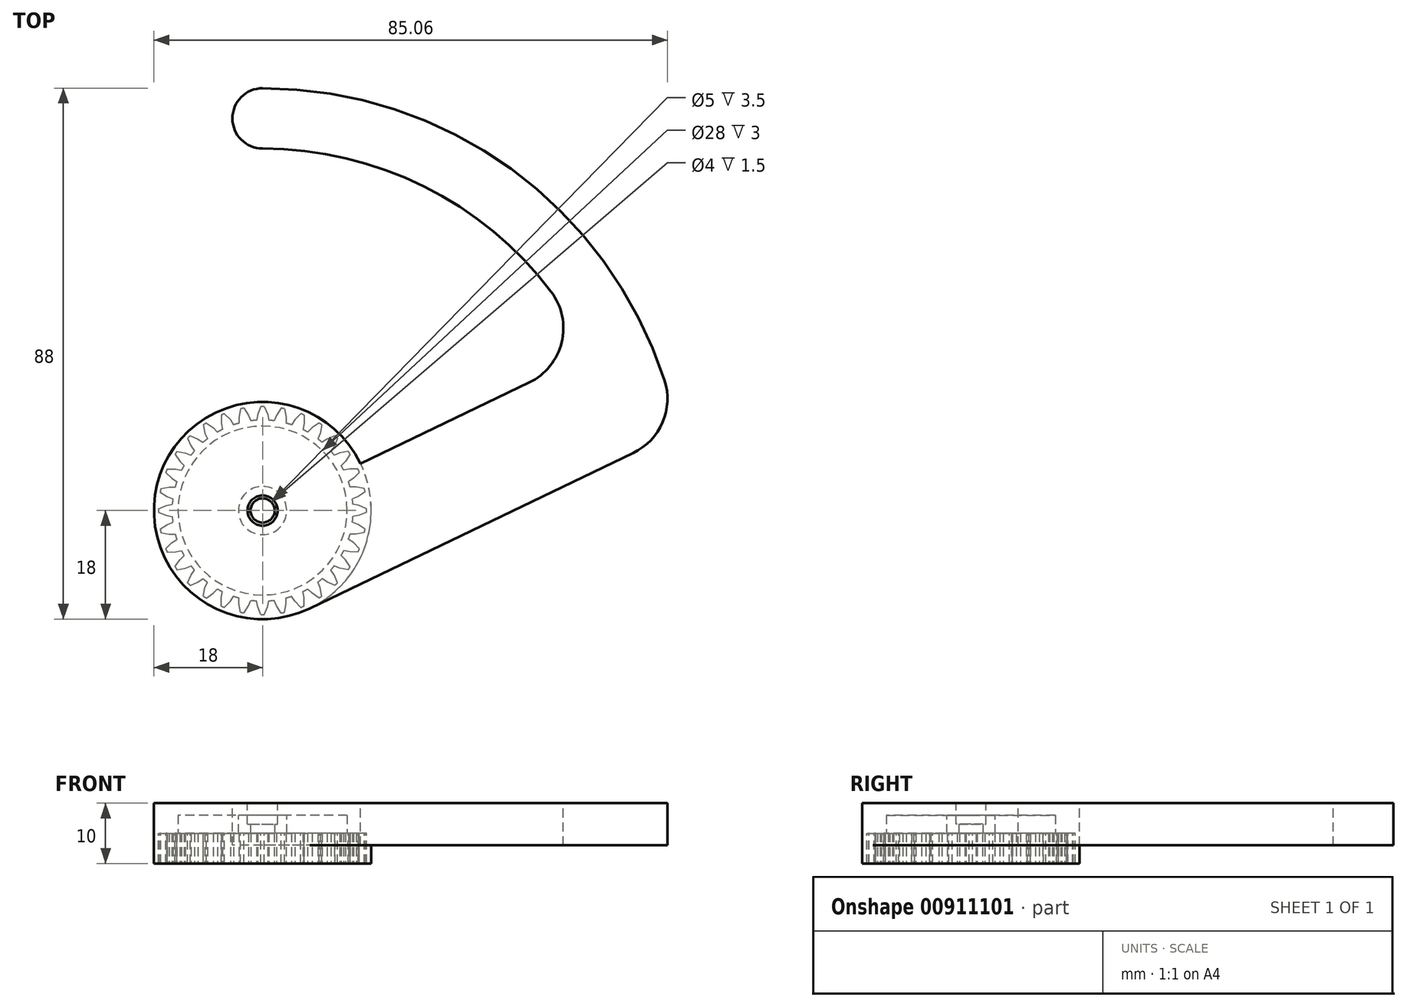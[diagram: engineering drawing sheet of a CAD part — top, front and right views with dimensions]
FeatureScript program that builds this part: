
annotation { "Feature Type Name" : "Feature", "Feature Type Description" : "" }
export const myFeature = defineFeature(function(context is Context, id is Id, definition is map)
    precondition{}
    {
        {
            var Q0;
            Q0=qCreatedBy(makeId("Top.planeOp"),FACE);
            var sketch = newSketch(context, id + "F0", { "sketchPlane" : qUnion([Q0])});
            skCircle(sketch, "E0", {"center": v(0, 0) * mm, "radius": 17.25 * mm});
            skCircle(sketch, "E1", {"center": v(0, 0) * mm, "radius": 15 * mm});
            skLineSegment(sketch, "E2", {"start": v(20.39, 0.01) * mm, "end": v(17.24, -0.58) * mm});
            skLineSegment(sketch, "E3", {"start": v(21.12, 1.29) * mm, "end": v(15.95, -0.82) * mm});
            skLineSegment(sketch, "E4", {"start": v(20.39, -0.02) * mm, "end": v(17.24, 0.58) * mm});
            skLineSegment(sketch, "E5", {"start": v(21.12, -1.29) * mm, "end": v(15.95, 0.82) * mm});
            skLineSegment(sketch, "E6", {"start": v(20, 4) * mm, "end": v(17.02, 2.8) * mm});
            skLineSegment(sketch, "E7", {"start": v(20.46, 5.38) * mm, "end": v(15.8, 2.3) * mm});
            skLineSegment(sketch, "E8", {"start": v(20, 3.96) * mm, "end": v(16.8, 3.93) * mm});
            skLineSegment(sketch, "E9", {"start": v(20.96, 2.85) * mm, "end": v(15.48, 3.92) * mm});
            skLineSegment(sketch, "E10", {"start": v(18.83, 7.81) * mm, "end": v(16.15, 6.06) * mm});
            skLineSegment(sketch, "E11", {"start": v(19.02, 9.27) * mm, "end": v(15.05, 5.34) * mm});
            skLineSegment(sketch, "E12", {"start": v(18.84, 7.79) * mm, "end": v(15.7, 7.13) * mm});
            skLineSegment(sketch, "E13", {"start": v(20, 6.89) * mm, "end": v(14.42, 6.86) * mm});
            skLineSegment(sketch, "E14", {"start": v(16.94, 11.34) * mm, "end": v(14.66, 9.1) * mm});
            skLineSegment(sketch, "E15", {"start": v(16.84, 12.8) * mm, "end": v(13.72, 8.18) * mm});
            skLineSegment(sketch, "E16", {"start": v(16.96, 11.31) * mm, "end": v(14.01, 10.06) * mm});
            skLineSegment(sketch, "E17", {"start": v(18.28, 10.66) * mm, "end": v(12.8, 9.54) * mm});
            skLineSegment(sketch, "E18", {"start": v(14.4, 14.43) * mm, "end": v(12.6, 11.78) * mm});
            skLineSegment(sketch, "E19", {"start": v(14.02, 15.84) * mm, "end": v(11.86, 10.7) * mm});
            skLineSegment(sketch, "E20", {"start": v(14.43, 14.4) * mm, "end": v(11.78, 12.6) * mm});
            skLineSegment(sketch, "E21", {"start": v(15.84, 14.02) * mm, "end": v(10.7, 11.86) * mm});
            skLineSegment(sketch, "E22", {"start": v(11.31, 16.96) * mm, "end": v(10.06, 14.01) * mm});
            skLineSegment(sketch, "E23", {"start": v(10.66, 18.28) * mm, "end": v(9.54, 12.8) * mm});
            skLineSegment(sketch, "E24", {"start": v(11.34, 16.94) * mm, "end": v(9.1, 14.66) * mm});
            skLineSegment(sketch, "E25", {"start": v(12.8, 16.84) * mm, "end": v(8.18, 13.72) * mm});
            skLineSegment(sketch, "E26", {"start": v(7.79, 18.84) * mm, "end": v(7.13, 15.7) * mm});
            skLineSegment(sketch, "E27", {"start": v(6.89, 20) * mm, "end": v(6.86, 14.42) * mm});
            skLineSegment(sketch, "E28", {"start": v(7.82, 18.83) * mm, "end": v(6.06, 16.15) * mm});
            skLineSegment(sketch, "E29", {"start": v(9.27, 19.02) * mm, "end": v(5.34, 15.05) * mm});
            skLineSegment(sketch, "E30", {"start": v(3.96, 20) * mm, "end": v(3.93, 16.8) * mm});
            skLineSegment(sketch, "E31", {"start": v(2.86, 20.96) * mm, "end": v(3.92, 15.48) * mm});
            skLineSegment(sketch, "E32", {"start": v(4, 20) * mm, "end": v(2.8, 17.02) * mm});
            skLineSegment(sketch, "E33", {"start": v(5.39, 20.46) * mm, "end": v(2.3, 15.8) * mm});
            skLineSegment(sketch, "E34", {"start": v(-0.01, 20.39) * mm, "end": v(0.58, 17.24) * mm});
            skLineSegment(sketch, "E35", {"start": v(-1.29, 21.12) * mm, "end": v(0.82, 15.95) * mm});
            skLineSegment(sketch, "E36", {"start": v(0.02, 20.39) * mm, "end": v(-0.58, 17.24) * mm});
            skLineSegment(sketch, "E37", {"start": v(1.3, 21.12) * mm, "end": v(-0.82, 15.95) * mm});
            skLineSegment(sketch, "E38", {"start": v(-4, 20) * mm, "end": v(-2.8, 17.02) * mm});
            skLineSegment(sketch, "E39", {"start": v(-5.38, 20.46) * mm, "end": v(-2.3, 15.8) * mm});
            skLineSegment(sketch, "E40", {"start": v(-3.96, 20) * mm, "end": v(-3.93, 16.8) * mm});
            skLineSegment(sketch, "E41", {"start": v(-2.85, 20.96) * mm, "end": v(-3.92, 15.48) * mm});
            skLineSegment(sketch, "E42", {"start": v(-7.82, 18.83) * mm, "end": v(-6.06, 16.15) * mm});
            skLineSegment(sketch, "E43", {"start": v(-9.27, 19.02) * mm, "end": v(-5.34, 15.05) * mm});
            skLineSegment(sketch, "E44", {"start": v(-7.79, 18.84) * mm, "end": v(-7.13, 15.7) * mm});
            skLineSegment(sketch, "E45", {"start": v(-6.89, 20) * mm, "end": v(-6.86, 14.42) * mm});
            skLineSegment(sketch, "E46", {"start": v(-11.34, 16.94) * mm, "end": v(-9.1, 14.66) * mm});
            skLineSegment(sketch, "E47", {"start": v(-12.8, 16.84) * mm, "end": v(-8.18, 13.72) * mm});
            skLineSegment(sketch, "E48", {"start": v(-11.31, 16.96) * mm, "end": v(-10.06, 14.01) * mm});
            skLineSegment(sketch, "E49", {"start": v(-10.66, 18.28) * mm, "end": v(-9.54, 12.8) * mm});
            skLineSegment(sketch, "E50", {"start": v(-14.43, 14.4) * mm, "end": v(-11.78, 12.6) * mm});
            skLineSegment(sketch, "E51", {"start": v(-15.84, 14.02) * mm, "end": v(-10.7, 11.86) * mm});
            skLineSegment(sketch, "E52", {"start": v(-14.4, 14.43) * mm, "end": v(-12.6, 11.78) * mm});
            skLineSegment(sketch, "E53", {"start": v(-14.02, 15.84) * mm, "end": v(-11.86, 10.7) * mm});
            skLineSegment(sketch, "E54", {"start": v(-16.96, 11.31) * mm, "end": v(-14.01, 10.06) * mm});
            skLineSegment(sketch, "E55", {"start": v(-18.27, 10.66) * mm, "end": v(-12.8, 9.54) * mm});
            skLineSegment(sketch, "E56", {"start": v(-16.94, 11.34) * mm, "end": v(-14.66, 9.1) * mm});
            skLineSegment(sketch, "E57", {"start": v(-16.84, 12.8) * mm, "end": v(-13.72, 8.18) * mm});
            skLineSegment(sketch, "E58", {"start": v(-18.84, 7.79) * mm, "end": v(-15.7, 7.13) * mm});
            skLineSegment(sketch, "E59", {"start": v(-20, 6.89) * mm, "end": v(-14.42, 6.86) * mm});
            skLineSegment(sketch, "E60", {"start": v(-18.83, 7.82) * mm, "end": v(-16.15, 6.06) * mm});
            skLineSegment(sketch, "E61", {"start": v(-19.02, 9.27) * mm, "end": v(-15.05, 5.34) * mm});
            skLineSegment(sketch, "E62", {"start": v(-20, 3.96) * mm, "end": v(-16.8, 3.93) * mm});
            skLineSegment(sketch, "E63", {"start": v(-20.96, 2.85) * mm, "end": v(-15.48, 3.92) * mm});
            skLineSegment(sketch, "E64", {"start": v(-20, 4) * mm, "end": v(-17.02, 2.8) * mm});
            skLineSegment(sketch, "E65", {"start": v(-20.46, 5.38) * mm, "end": v(-15.8, 2.3) * mm});
            skLineSegment(sketch, "E66", {"start": v(-20.39, -0.02) * mm, "end": v(-17.24, 0.58) * mm});
            skLineSegment(sketch, "E67", {"start": v(-21.12, -1.29) * mm, "end": v(-15.95, 0.82) * mm});
            skLineSegment(sketch, "E68", {"start": v(-20.39, 0.01) * mm, "end": v(-17.24, -0.58) * mm});
            skLineSegment(sketch, "E69", {"start": v(-21.12, 1.29) * mm, "end": v(-15.95, -0.82) * mm});
            skLineSegment(sketch, "E70", {"start": v(-20, -4) * mm, "end": v(-17.02, -2.8) * mm});
            skLineSegment(sketch, "E71", {"start": v(-20.46, -5.38) * mm, "end": v(-15.8, -2.3) * mm});
            skLineSegment(sketch, "E72", {"start": v(-20, -3.96) * mm, "end": v(-16.8, -3.93) * mm});
            skLineSegment(sketch, "E73", {"start": v(-20.96, -2.85) * mm, "end": v(-15.48, -3.92) * mm});
            skLineSegment(sketch, "E74", {"start": v(-18.83, -7.81) * mm, "end": v(-16.15, -6.06) * mm});
            skLineSegment(sketch, "E75", {"start": v(-19.02, -9.27) * mm, "end": v(-15.05, -5.34) * mm});
            skLineSegment(sketch, "E76", {"start": v(-18.84, -7.79) * mm, "end": v(-15.7, -7.13) * mm});
            skLineSegment(sketch, "E77", {"start": v(-20, -6.89) * mm, "end": v(-14.42, -6.86) * mm});
            skLineSegment(sketch, "E78", {"start": v(-16.94, -11.34) * mm, "end": v(-14.66, -9.1) * mm});
            skLineSegment(sketch, "E79", {"start": v(-16.84, -12.8) * mm, "end": v(-13.72, -8.18) * mm});
            skLineSegment(sketch, "E80", {"start": v(-16.96, -11.31) * mm, "end": v(-14.01, -10.06) * mm});
            skLineSegment(sketch, "E81", {"start": v(-18.27, -10.66) * mm, "end": v(-12.8, -9.54) * mm});
            skLineSegment(sketch, "E82", {"start": v(-14.4, -14.43) * mm, "end": v(-12.6, -11.78) * mm});
            skLineSegment(sketch, "E83", {"start": v(-14.02, -15.84) * mm, "end": v(-11.86, -10.7) * mm});
            skLineSegment(sketch, "E84", {"start": v(-14.43, -14.4) * mm, "end": v(-11.78, -12.6) * mm});
            skLineSegment(sketch, "E85", {"start": v(-15.84, -14.02) * mm, "end": v(-10.7, -11.86) * mm});
            skLineSegment(sketch, "E86", {"start": v(-11.31, -16.96) * mm, "end": v(-10.06, -14.01) * mm});
            skLineSegment(sketch, "E87", {"start": v(-10.66, -18.27) * mm, "end": v(-9.54, -12.8) * mm});
            skLineSegment(sketch, "E88", {"start": v(-11.34, -16.94) * mm, "end": v(-9.1, -14.66) * mm});
            skLineSegment(sketch, "E89", {"start": v(-12.8, -16.84) * mm, "end": v(-8.18, -13.72) * mm});
            skLineSegment(sketch, "E90", {"start": v(-7.79, -18.84) * mm, "end": v(-7.13, -15.7) * mm});
            skLineSegment(sketch, "E91", {"start": v(-6.89, -20) * mm, "end": v(-6.86, -14.42) * mm});
            skLineSegment(sketch, "E92", {"start": v(-7.81, -18.83) * mm, "end": v(-6.06, -16.15) * mm});
            skLineSegment(sketch, "E93", {"start": v(-9.27, -19.02) * mm, "end": v(-5.34, -15.05) * mm});
            skLineSegment(sketch, "E94", {"start": v(-3.96, -20) * mm, "end": v(-3.93, -16.8) * mm});
            skLineSegment(sketch, "E95", {"start": v(-2.86, -20.96) * mm, "end": v(-3.92, -15.48) * mm});
            skLineSegment(sketch, "E96", {"start": v(-4, -20) * mm, "end": v(-2.8, -17.02) * mm});
            skLineSegment(sketch, "E97", {"start": v(-5.38, -20.46) * mm, "end": v(-2.3, -15.8) * mm});
            skLineSegment(sketch, "E98", {"start": v(0.02, -20.39) * mm, "end": v(-0.58, -17.24) * mm});
            skLineSegment(sketch, "E99", {"start": v(1.29, -21.12) * mm, "end": v(-0.82, -15.95) * mm});
            skLineSegment(sketch, "E100", {"start": v(-0.01, -20.39) * mm, "end": v(0.58, -17.24) * mm});
            skLineSegment(sketch, "E101", {"start": v(-1.29, -21.12) * mm, "end": v(0.82, -15.95) * mm});
            skLineSegment(sketch, "E102", {"start": v(4, -20) * mm, "end": v(2.8, -17.02) * mm});
            skLineSegment(sketch, "E103", {"start": v(5.38, -20.46) * mm, "end": v(2.3, -15.8) * mm});
            skLineSegment(sketch, "E104", {"start": v(3.96, -20) * mm, "end": v(3.93, -16.8) * mm});
            skLineSegment(sketch, "E105", {"start": v(2.86, -20.96) * mm, "end": v(3.92, -15.48) * mm});
            skLineSegment(sketch, "E106", {"start": v(7.82, -18.83) * mm, "end": v(6.06, -16.15) * mm});
            skLineSegment(sketch, "E107", {"start": v(9.27, -19.02) * mm, "end": v(5.34, -15.05) * mm});
            skLineSegment(sketch, "E108", {"start": v(7.79, -18.84) * mm, "end": v(7.13, -15.7) * mm});
            skLineSegment(sketch, "E109", {"start": v(6.89, -20) * mm, "end": v(6.86, -14.42) * mm});
            skLineSegment(sketch, "E110", {"start": v(11.34, -16.94) * mm, "end": v(9.1, -14.66) * mm});
            skLineSegment(sketch, "E111", {"start": v(12.8, -16.84) * mm, "end": v(8.18, -13.72) * mm});
            skLineSegment(sketch, "E112", {"start": v(11.31, -16.96) * mm, "end": v(10.06, -14.01) * mm});
            skLineSegment(sketch, "E113", {"start": v(10.66, -18.28) * mm, "end": v(9.54, -12.8) * mm});
            skLineSegment(sketch, "E114", {"start": v(14.43, -14.4) * mm, "end": v(11.78, -12.6) * mm});
            skLineSegment(sketch, "E115", {"start": v(15.84, -14.02) * mm, "end": v(10.7, -11.86) * mm});
            skLineSegment(sketch, "E116", {"start": v(14.4, -14.43) * mm, "end": v(12.6, -11.78) * mm});
            skLineSegment(sketch, "E117", {"start": v(14.02, -15.84) * mm, "end": v(11.86, -10.7) * mm});
            skLineSegment(sketch, "E118", {"start": v(16.96, -11.31) * mm, "end": v(14.01, -10.06) * mm});
            skLineSegment(sketch, "E119", {"start": v(18.27, -10.66) * mm, "end": v(12.8, -9.54) * mm});
            skLineSegment(sketch, "E120", {"start": v(16.94, -11.34) * mm, "end": v(14.66, -9.1) * mm});
            skLineSegment(sketch, "E121", {"start": v(16.84, -12.8) * mm, "end": v(13.72, -8.18) * mm});
            skLineSegment(sketch, "E122", {"start": v(18.84, -7.79) * mm, "end": v(15.7, -7.13) * mm});
            skLineSegment(sketch, "E123", {"start": v(20, -6.89) * mm, "end": v(14.42, -6.86) * mm});
            skLineSegment(sketch, "E124", {"start": v(18.83, -7.81) * mm, "end": v(16.15, -6.06) * mm});
            skLineSegment(sketch, "E125", {"start": v(19.02, -9.27) * mm, "end": v(15.05, -5.34) * mm});
            skLineSegment(sketch, "E126", {"start": v(20, -3.96) * mm, "end": v(16.8, -3.93) * mm});
            skLineSegment(sketch, "E127", {"start": v(20.96, -2.86) * mm, "end": v(15.48, -3.92) * mm});
            skLineSegment(sketch, "E128", {"start": v(20, -4) * mm, "end": v(17.02, -2.8) * mm});
            skLineSegment(sketch, "E129", {"start": v(20.46, -5.38) * mm, "end": v(15.8, -2.3) * mm});
            skLineSegment(sketch, "E130.trimOffspring", {"start": v(-6.86, 14.42) * mm, "end": v(-5.74, 9.05) * mm});
            skLineSegment(sketch, "E131.trimOffspring", {"start": v(-6.86, 13.34) * mm, "end": v(-6.84, 10) * mm});
            skLineSegment(sketch, "E132.trimOffspring", {"start": v(-5.34, 15.05) * mm, "end": v(-2.34, 10.46) * mm});
            skLineSegment(sketch, "E133.trimOffspring", {"start": v(-4.58, 14.28) * mm, "end": v(-2.23, 11.91) * mm});
            skLineSegment(sketch, "E134.trimOffspring", {"start": v(-3.92, 15.48) * mm, "end": v(-3.87, 10) * mm});
            skLineSegment(sketch, "E135.trimOffspring", {"start": v(-4.12, 14.42) * mm, "end": v(-4.76, 11.15) * mm});
            skLineSegment(sketch, "E136.trimOffspring", {"start": v(-7.28, 13.11) * mm, "end": v(-4.52, 11.25) * mm});
            skLineSegment(sketch, "E137.trimOffspring", {"start": v(-8.18, 13.72) * mm, "end": v(-4.34, 9.8) * mm});
            skLineSegment(sketch, "E138.trimOffspring", {"start": v(-2.3, 15.8) * mm, "end": v(-0.25, 10.72) * mm});
            skLineSegment(sketch, "E139.trimOffspring", {"start": v(-1.7, 14.9) * mm, "end": v(0.13, 12.12) * mm});
            skLineSegment(sketch, "E140.trimOffspring", {"start": v(-0.82, 15.95) * mm, "end": v(-1.84, 10.56) * mm});
            skLineSegment(sketch, "E141.trimOffspring", {"start": v(-1.23, 14.95) * mm, "end": v(-2.5, 11.86) * mm});
            skLineSegment(sketch, "E142.trimOffspring", {"start": v(0.82, 15.95) * mm, "end": v(1.84, 10.56) * mm});
            skLineSegment(sketch, "E143.trimOffspring", {"start": v(1.23, 14.95) * mm, "end": v(2.5, 11.86) * mm});
            skLineSegment(sketch, "E144.trimOffspring", {"start": v(1.7, 14.9) * mm, "end": v(-0.13, 12.12) * mm});
            skLineSegment(sketch, "E145.trimOffspring", {"start": v(2.3, 15.8) * mm, "end": v(0.26, 10.72) * mm});
            skLineSegment(sketch, "E146.trimOffspring", {"start": v(3.92, 15.48) * mm, "end": v(3.87, 10) * mm});
            skLineSegment(sketch, "E147.trimOffspring", {"start": v(4.12, 14.42) * mm, "end": v(4.76, 11.15) * mm});
            skLineSegment(sketch, "E148.trimOffspring", {"start": v(4.58, 14.28) * mm, "end": v(2.23, 11.91) * mm});
            skLineSegment(sketch, "E149.trimOffspring", {"start": v(5.34, 15.05) * mm, "end": v(2.34, 10.46) * mm});
            skLineSegment(sketch, "E150.trimOffspring", {"start": v(6.86, 14.42) * mm, "end": v(5.74, 9.05) * mm});
            skLineSegment(sketch, "E151.trimOffspring", {"start": v(6.86, 13.34) * mm, "end": v(6.84, 10) * mm});
            skLineSegment(sketch, "E152.trimOffspring", {"start": v(7.28, 13.11) * mm, "end": v(4.52, 11.25) * mm});
            skLineSegment(sketch, "E153.trimOffspring", {"start": v(8.18, 13.72) * mm, "end": v(4.34, 9.8) * mm});
            skLineSegment(sketch, "E154.trimOffspring", {"start": v(9.54, 12.8) * mm, "end": v(7.4, 7.76) * mm});
            skLineSegment(sketch, "E155.trimOffspring", {"start": v(9.33, 11.75) * mm, "end": v(8.66, 8.48) * mm});
            skLineSegment(sketch, "E156.trimOffspring", {"start": v(9.7, 11.44) * mm, "end": v(6.62, 10.15) * mm});
            skLineSegment(sketch, "E157.trimOffspring", {"start": v(10.7, 11.86) * mm, "end": v(6.17, 8.77) * mm});
            skLineSegment(sketch, "E158.trimOffspring", {"start": v(11.86, 10.7) * mm, "end": v(8.77, 6.16) * mm});
            skLineSegment(sketch, "E159.trimOffspring", {"start": v(11.44, 9.7) * mm, "end": v(10.15, 6.62) * mm});
            skLineSegment(sketch, "E160.trimOffspring", {"start": v(11.75, 9.33) * mm, "end": v(8.48, 8.66) * mm});
            skLineSegment(sketch, "E161.trimOffspring", {"start": v(12.8, 9.54) * mm, "end": v(7.76, 7.4) * mm});
            skLineSegment(sketch, "E162.trimOffspring", {"start": v(-9.54, 12.8) * mm, "end": v(-7.4, 7.76) * mm});
            skLineSegment(sketch, "E163.trimOffspring", {"start": v(-9.33, 11.75) * mm, "end": v(-8.66, 8.48) * mm});
            skLineSegment(sketch, "E164.trimOffspring", {"start": v(-10.7, 11.86) * mm, "end": v(-6.16, 8.77) * mm});
            skLineSegment(sketch, "E165.trimOffspring", {"start": v(-9.7, 11.44) * mm, "end": v(-6.62, 10.15) * mm});
            skLineSegment(sketch, "E166.trimOffspring", {"start": v(-11.86, 10.7) * mm, "end": v(-8.77, 6.17) * mm});
            skLineSegment(sketch, "E167.trimOffspring", {"start": v(-11.44, 9.7) * mm, "end": v(-10.15, 6.62) * mm});
            skLineSegment(sketch, "E168.trimOffspring", {"start": v(-11.75, 9.33) * mm, "end": v(-8.48, 8.66) * mm});
            skLineSegment(sketch, "E169.trimOffspring", {"start": v(-12.8, 9.54) * mm, "end": v(-7.76, 7.4) * mm});
            skLineSegment(sketch, "E170.trimOffspring", {"start": v(-13.72, 8.18) * mm, "end": v(-9.8, 4.34) * mm});
            skLineSegment(sketch, "E171.trimOffspring", {"start": v(-13.11, 7.28) * mm, "end": v(-11.25, 4.52) * mm});
            skLineSegment(sketch, "E172.trimOffspring", {"start": v(-13.34, 6.86) * mm, "end": v(-10, 6.84) * mm});
            skLineSegment(sketch, "E173.trimOffspring", {"start": v(-14.42, 6.86) * mm, "end": v(-9.05, 5.74) * mm});
            skLineSegment(sketch, "E174.trimOffspring", {"start": v(-14.28, 4.58) * mm, "end": v(-11.91, 2.23) * mm});
            skLineSegment(sketch, "E175.trimOffspring", {"start": v(-15.05, 5.34) * mm, "end": v(-10.46, 2.34) * mm});
            skLineSegment(sketch, "E176.trimOffspring", {"start": v(-14.42, 4.12) * mm, "end": v(-11.15, 4.76) * mm});
            skLineSegment(sketch, "E177.trimOffspring", {"start": v(-15.48, 3.92) * mm, "end": v(-10, 3.87) * mm});
            skLineSegment(sketch, "E178.trimOffspring", {"start": v(-14.9, 1.7) * mm, "end": v(-12.12, -0.13) * mm});
            skLineSegment(sketch, "E179.trimOffspring", {"start": v(-15.8, 2.3) * mm, "end": v(-10.72, 0.25) * mm});
            skLineSegment(sketch, "E180.trimOffspring", {"start": v(-15.95, 0.82) * mm, "end": v(-10.56, 1.84) * mm});
            skLineSegment(sketch, "E181.trimOffspring", {"start": v(-14.95, 1.23) * mm, "end": v(-11.86, 2.5) * mm});
            skLineSegment(sketch, "E182.trimOffspring", {"start": v(13.72, 8.18) * mm, "end": v(9.8, 4.34) * mm});
            skLineSegment(sketch, "E183.trimOffspring", {"start": v(13.11, 7.28) * mm, "end": v(11.25, 4.52) * mm});
            skLineSegment(sketch, "E184.trimOffspring", {"start": v(13.34, 6.86) * mm, "end": v(10, 6.84) * mm});
            skLineSegment(sketch, "E185.trimOffspring", {"start": v(14.42, 6.86) * mm, "end": v(9.05, 5.74) * mm});
            skLineSegment(sketch, "E186.trimOffspring", {"start": v(15.05, 5.34) * mm, "end": v(10.46, 2.34) * mm});
            skLineSegment(sketch, "E187.trimOffspring", {"start": v(14.28, 4.58) * mm, "end": v(11.91, 2.23) * mm});
            skLineSegment(sketch, "E188.trimOffspring", {"start": v(14.42, 4.12) * mm, "end": v(11.15, 4.76) * mm});
            skLineSegment(sketch, "E189.trimOffspring", {"start": v(15.48, 3.92) * mm, "end": v(10, 3.87) * mm});
            skLineSegment(sketch, "E190.trimOffspring", {"start": v(15.8, 2.3) * mm, "end": v(10.72, 0.25) * mm});
            skLineSegment(sketch, "E191.trimOffspring", {"start": v(14.9, 1.7) * mm, "end": v(12.12, -0.13) * mm});
            skLineSegment(sketch, "E192.trimOffspring", {"start": v(14.95, 1.23) * mm, "end": v(11.86, 2.5) * mm});
            skLineSegment(sketch, "E193.trimOffspring", {"start": v(15.95, 0.82) * mm, "end": v(10.56, 1.84) * mm});
            skLineSegment(sketch, "E194.trimOffspring", {"start": v(15.95, -0.82) * mm, "end": v(10.56, -1.84) * mm});
            skLineSegment(sketch, "E195.trimOffspring", {"start": v(14.95, -1.23) * mm, "end": v(11.86, -2.5) * mm});
            skLineSegment(sketch, "E196.trimOffspring", {"start": v(14.9, -1.7) * mm, "end": v(12.12, 0.13) * mm});
            skLineSegment(sketch, "E197.trimOffspring", {"start": v(15.8, -2.3) * mm, "end": v(10.72, -0.25) * mm});
            skLineSegment(sketch, "E198.trimOffspring", {"start": v(15.48, -3.92) * mm, "end": v(10, -3.87) * mm});
            skLineSegment(sketch, "E199.trimOffspring", {"start": v(14.42, -4.12) * mm, "end": v(11.15, -4.76) * mm});
            skLineSegment(sketch, "E200.trimOffspring", {"start": v(14.28, -4.58) * mm, "end": v(11.91, -2.24) * mm});
            skLineSegment(sketch, "E201.trimOffspring", {"start": v(15.05, -5.34) * mm, "end": v(10.46, -2.34) * mm});
            skLineSegment(sketch, "E202.trimOffspring", {"start": v(14.42, -6.86) * mm, "end": v(9.05, -5.74) * mm});
            skLineSegment(sketch, "E203.trimOffspring", {"start": v(13.34, -6.86) * mm, "end": v(10, -6.84) * mm});
            skLineSegment(sketch, "E204.trimOffspring", {"start": v(13.11, -7.28) * mm, "end": v(11.25, -4.52) * mm});
            skLineSegment(sketch, "E205.trimOffspring", {"start": v(13.72, -8.18) * mm, "end": v(9.8, -4.34) * mm});
            skLineSegment(sketch, "E206.trimOffspring", {"start": v(12.8, -9.54) * mm, "end": v(7.76, -7.4) * mm});
            skLineSegment(sketch, "E207.trimOffspring", {"start": v(11.75, -9.33) * mm, "end": v(8.48, -8.66) * mm});
            skLineSegment(sketch, "E208.trimOffspring", {"start": v(11.44, -9.7) * mm, "end": v(10.15, -6.62) * mm});
            skLineSegment(sketch, "E209.trimOffspring", {"start": v(11.86, -10.7) * mm, "end": v(8.77, -6.17) * mm});
            skLineSegment(sketch, "E210.trimOffspring", {"start": v(9.7, -11.44) * mm, "end": v(6.62, -10.15) * mm});
            skLineSegment(sketch, "E211.trimOffspring", {"start": v(10.7, -11.86) * mm, "end": v(6.17, -8.77) * mm});
            skLineSegment(sketch, "E212.trimOffspring", {"start": v(9.33, -11.75) * mm, "end": v(8.66, -8.48) * mm});
            skLineSegment(sketch, "E213.trimOffspring", {"start": v(9.54, -12.8) * mm, "end": v(7.4, -7.76) * mm});
            skLineSegment(sketch, "E214.trimOffspring", {"start": v(7.28, -13.11) * mm, "end": v(4.52, -11.25) * mm});
            skLineSegment(sketch, "E215.trimOffspring", {"start": v(8.18, -13.72) * mm, "end": v(4.34, -9.8) * mm});
            skLineSegment(sketch, "E216.trimOffspring", {"start": v(6.86, -13.34) * mm, "end": v(6.84, -10) * mm});
            skLineSegment(sketch, "E217.trimOffspring", {"start": v(6.86, -14.42) * mm, "end": v(5.74, -9.05) * mm});
            skLineSegment(sketch, "E218.trimOffspring", {"start": v(4.58, -14.28) * mm, "end": v(2.24, -11.91) * mm});
            skLineSegment(sketch, "E219.trimOffspring", {"start": v(5.34, -15.05) * mm, "end": v(2.34, -10.46) * mm});
            skLineSegment(sketch, "E220.trimOffspring", {"start": v(4.12, -14.42) * mm, "end": v(4.76, -11.15) * mm});
            skLineSegment(sketch, "E221.trimOffspring", {"start": v(3.92, -15.48) * mm, "end": v(3.86, -10) * mm});
            skLineSegment(sketch, "E222.trimOffspring", {"start": v(1.7, -14.9) * mm, "end": v(-0.13, -12.12) * mm});
            skLineSegment(sketch, "E223.trimOffspring", {"start": v(2.3, -15.8) * mm, "end": v(0.26, -10.72) * mm});
            skLineSegment(sketch, "E224.trimOffspring", {"start": v(1.23, -14.95) * mm, "end": v(2.5, -11.86) * mm});
            skLineSegment(sketch, "E225.trimOffspring", {"start": v(0.82, -15.95) * mm, "end": v(1.84, -10.56) * mm});
            skLineSegment(sketch, "E226.trimOffspring", {"start": v(-0.82, -15.95) * mm, "end": v(-1.84, -10.56) * mm});
            skLineSegment(sketch, "E227.trimOffspring", {"start": v(-1.23, -14.95) * mm, "end": v(-2.5, -11.86) * mm});
            skLineSegment(sketch, "E228.trimOffspring", {"start": v(-1.7, -14.9) * mm, "end": v(0.13, -12.12) * mm});
            skLineSegment(sketch, "E229.trimOffspring", {"start": v(-2.3, -15.8) * mm, "end": v(-0.26, -10.72) * mm});
            skLineSegment(sketch, "E230.trimOffspring", {"start": v(-15.95, -0.82) * mm, "end": v(-10.56, -1.84) * mm});
            skLineSegment(sketch, "E231.trimOffspring", {"start": v(-14.95, -1.23) * mm, "end": v(-11.86, -2.5) * mm});
            skLineSegment(sketch, "E232.trimOffspring", {"start": v(-14.9, -1.7) * mm, "end": v(-12.12, 0.13) * mm});
            skLineSegment(sketch, "E233.trimOffspring", {"start": v(-15.8, -2.3) * mm, "end": v(-10.72, -0.25) * mm});
            skLineSegment(sketch, "E234.trimOffspring", {"start": v(-14.42, -4.12) * mm, "end": v(-11.15, -4.76) * mm});
            skLineSegment(sketch, "E235.trimOffspring", {"start": v(-15.48, -3.92) * mm, "end": v(-10, -3.86) * mm});
            skLineSegment(sketch, "E236.trimOffspring", {"start": v(-15.05, -5.34) * mm, "end": v(-10.46, -2.34) * mm});
            skLineSegment(sketch, "E237.trimOffspring", {"start": v(-14.28, -4.58) * mm, "end": v(-11.91, -2.24) * mm});
            skLineSegment(sketch, "E238.trimOffspring", {"start": v(-14.42, -6.86) * mm, "end": v(-9.05, -5.74) * mm});
            skLineSegment(sketch, "E239.trimOffspring", {"start": v(-13.34, -6.86) * mm, "end": v(-10, -6.84) * mm});
            skLineSegment(sketch, "E240.trimOffspring", {"start": v(-13.11, -7.28) * mm, "end": v(-11.25, -4.52) * mm});
            skLineSegment(sketch, "E241.trimOffspring", {"start": v(-13.72, -8.18) * mm, "end": v(-9.8, -4.34) * mm});
            skLineSegment(sketch, "E242.trimOffspring", {"start": v(-12.8, -9.54) * mm, "end": v(-7.76, -7.4) * mm});
            skLineSegment(sketch, "E243.trimOffspring", {"start": v(-11.75, -9.33) * mm, "end": v(-8.48, -8.66) * mm});
            skLineSegment(sketch, "E244.trimOffspring", {"start": v(-11.44, -9.7) * mm, "end": v(-10.15, -6.62) * mm});
            skLineSegment(sketch, "E245.trimOffspring", {"start": v(-11.86, -10.7) * mm, "end": v(-8.77, -6.16) * mm});
            skLineSegment(sketch, "E246.trimOffspring", {"start": v(-10.7, -11.86) * mm, "end": v(-6.17, -8.77) * mm});
            skLineSegment(sketch, "E247.trimOffspring", {"start": v(-9.7, -11.44) * mm, "end": v(-6.62, -10.15) * mm});
            skLineSegment(sketch, "E248.trimOffspring", {"start": v(-9.33, -11.75) * mm, "end": v(-8.66, -8.48) * mm});
            skLineSegment(sketch, "E249.trimOffspring", {"start": v(-9.54, -12.8) * mm, "end": v(-7.4, -7.76) * mm});
            skLineSegment(sketch, "E250.trimOffspring", {"start": v(-8.18, -13.72) * mm, "end": v(-4.34, -9.8) * mm});
            skLineSegment(sketch, "E251.trimOffspring", {"start": v(-7.28, -13.11) * mm, "end": v(-4.52, -11.25) * mm});
            skLineSegment(sketch, "E252.trimOffspring", {"start": v(-6.86, -13.34) * mm, "end": v(-6.84, -10) * mm});
            skLineSegment(sketch, "E253.trimOffspring", {"start": v(-6.86, -14.42) * mm, "end": v(-5.74, -9.05) * mm});
            skLineSegment(sketch, "E254.trimOffspring", {"start": v(-5.34, -15.05) * mm, "end": v(-2.34, -10.46) * mm});
            skLineSegment(sketch, "E255.trimOffspring", {"start": v(-4.58, -14.28) * mm, "end": v(-2.23, -11.91) * mm});
            skLineSegment(sketch, "E256.trimOffspring", {"start": v(-4.12, -14.42) * mm, "end": v(-4.76, -11.15) * mm});
            skLineSegment(sketch, "E257.trimOffspring", {"start": v(-3.92, -15.48) * mm, "end": v(-3.87, -10) * mm});
            skSolve(sketch);
        }
        {
            var Q0;
            Q0 = qSketchRegion(id + "F0", true);
            extrude(context, id + "F1", {"entities" : qUnion([Q0]), "depth" : 5 * mm, "offsetDistance" : 25 * mm});
        }
        {
            var Q0;
            Q0=makeQuery(id+"F1.opExtrude","CAP_FACE",FACE,{"disambiguationData":[OSD([sQuery(id+"F0.wireOp",EDGE,"E0"),sQuery(id+"F0.wireOp",EDGE,"E1"),sQuery(id+"F0.wireOp",EDGE,"E2"),sQuery(id+"F0.wireOp",EDGE,"E3"),sQuery(id+"F0.wireOp",EDGE,"E4"),sQuery(id+"F0.wireOp",EDGE,"E5"),sQuery(id+"F0.wireOp",EDGE,"E6"),sQuery(id+"F0.wireOp",EDGE,"E7"),sQuery(id+"F0.wireOp",EDGE,"E8"),sQuery(id+"F0.wireOp",EDGE,"E9"),sQuery(id+"F0.wireOp",EDGE,"E10"),sQuery(id+"F0.wireOp",EDGE,"E11"),sQuery(id+"F0.wireOp",EDGE,"E12"),sQuery(id+"F0.wireOp",EDGE,"E13"),sQuery(id+"F0.wireOp",EDGE,"E14"),sQuery(id+"F0.wireOp",EDGE,"E15"),sQuery(id+"F0.wireOp",EDGE,"E16"),sQuery(id+"F0.wireOp",EDGE,"E17"),sQuery(id+"F0.wireOp",EDGE,"E18"),sQuery(id+"F0.wireOp",EDGE,"E19"),sQuery(id+"F0.wireOp",EDGE,"E20"),sQuery(id+"F0.wireOp",EDGE,"E21"),sQuery(id+"F0.wireOp",EDGE,"E22"),sQuery(id+"F0.wireOp",EDGE,"E23"),sQuery(id+"F0.wireOp",EDGE,"E24"),sQuery(id+"F0.wireOp",EDGE,"E25"),sQuery(id+"F0.wireOp",EDGE,"E26"),sQuery(id+"F0.wireOp",EDGE,"E27"),sQuery(id+"F0.wireOp",EDGE,"E28"),sQuery(id+"F0.wireOp",EDGE,"E29"),sQuery(id+"F0.wireOp",EDGE,"E30"),sQuery(id+"F0.wireOp",EDGE,"E31"),sQuery(id+"F0.wireOp",EDGE,"E32"),sQuery(id+"F0.wireOp",EDGE,"E33"),sQuery(id+"F0.wireOp",EDGE,"E34"),sQuery(id+"F0.wireOp",EDGE,"E35"),sQuery(id+"F0.wireOp",EDGE,"E36"),sQuery(id+"F0.wireOp",EDGE,"E37"),sQuery(id+"F0.wireOp",EDGE,"E38"),sQuery(id+"F0.wireOp",EDGE,"E39"),sQuery(id+"F0.wireOp",EDGE,"E40"),sQuery(id+"F0.wireOp",EDGE,"E41"),sQuery(id+"F0.wireOp",EDGE,"E42"),sQuery(id+"F0.wireOp",EDGE,"E43"),sQuery(id+"F0.wireOp",EDGE,"E44"),sQuery(id+"F0.wireOp",EDGE,"E45"),sQuery(id+"F0.wireOp",EDGE,"E46"),sQuery(id+"F0.wireOp",EDGE,"E47"),sQuery(id+"F0.wireOp",EDGE,"E48"),sQuery(id+"F0.wireOp",EDGE,"E49"),sQuery(id+"F0.wireOp",EDGE,"E50"),sQuery(id+"F0.wireOp",EDGE,"E51"),sQuery(id+"F0.wireOp",EDGE,"E52"),sQuery(id+"F0.wireOp",EDGE,"E53"),sQuery(id+"F0.wireOp",EDGE,"E54"),sQuery(id+"F0.wireOp",EDGE,"E55"),sQuery(id+"F0.wireOp",EDGE,"E56"),sQuery(id+"F0.wireOp",EDGE,"E57"),sQuery(id+"F0.wireOp",EDGE,"E58"),sQuery(id+"F0.wireOp",EDGE,"E59"),sQuery(id+"F0.wireOp",EDGE,"E60"),sQuery(id+"F0.wireOp",EDGE,"E61"),sQuery(id+"F0.wireOp",EDGE,"E62"),sQuery(id+"F0.wireOp",EDGE,"E63"),sQuery(id+"F0.wireOp",EDGE,"E64"),sQuery(id+"F0.wireOp",EDGE,"E65"),sQuery(id+"F0.wireOp",EDGE,"E66"),sQuery(id+"F0.wireOp",EDGE,"E67"),sQuery(id+"F0.wireOp",EDGE,"E68"),sQuery(id+"F0.wireOp",EDGE,"E69"),sQuery(id+"F0.wireOp",EDGE,"E70"),sQuery(id+"F0.wireOp",EDGE,"E71"),sQuery(id+"F0.wireOp",EDGE,"E72"),sQuery(id+"F0.wireOp",EDGE,"E73"),sQuery(id+"F0.wireOp",EDGE,"E74"),sQuery(id+"F0.wireOp",EDGE,"E75"),sQuery(id+"F0.wireOp",EDGE,"E76"),sQuery(id+"F0.wireOp",EDGE,"E77"),sQuery(id+"F0.wireOp",EDGE,"E78"),sQuery(id+"F0.wireOp",EDGE,"E79"),sQuery(id+"F0.wireOp",EDGE,"E80"),sQuery(id+"F0.wireOp",EDGE,"E81"),sQuery(id+"F0.wireOp",EDGE,"E82"),sQuery(id+"F0.wireOp",EDGE,"E83"),sQuery(id+"F0.wireOp",EDGE,"E84"),sQuery(id+"F0.wireOp",EDGE,"E85"),sQuery(id+"F0.wireOp",EDGE,"E86"),sQuery(id+"F0.wireOp",EDGE,"E87"),sQuery(id+"F0.wireOp",EDGE,"E88"),sQuery(id+"F0.wireOp",EDGE,"E89"),sQuery(id+"F0.wireOp",EDGE,"E90"),sQuery(id+"F0.wireOp",EDGE,"E91"),sQuery(id+"F0.wireOp",EDGE,"E92"),sQuery(id+"F0.wireOp",EDGE,"E93"),sQuery(id+"F0.wireOp",EDGE,"E94"),sQuery(id+"F0.wireOp",EDGE,"E95"),sQuery(id+"F0.wireOp",EDGE,"E96"),sQuery(id+"F0.wireOp",EDGE,"E97"),sQuery(id+"F0.wireOp",EDGE,"E98"),sQuery(id+"F0.wireOp",EDGE,"E99"),sQuery(id+"F0.wireOp",EDGE,"E100"),sQuery(id+"F0.wireOp",EDGE,"E101"),sQuery(id+"F0.wireOp",EDGE,"E102"),sQuery(id+"F0.wireOp",EDGE,"E103"),sQuery(id+"F0.wireOp",EDGE,"E104"),sQuery(id+"F0.wireOp",EDGE,"E105"),sQuery(id+"F0.wireOp",EDGE,"E106"),sQuery(id+"F0.wireOp",EDGE,"E107"),sQuery(id+"F0.wireOp",EDGE,"E108"),sQuery(id+"F0.wireOp",EDGE,"E109"),sQuery(id+"F0.wireOp",EDGE,"E110"),sQuery(id+"F0.wireOp",EDGE,"E111"),sQuery(id+"F0.wireOp",EDGE,"E112"),sQuery(id+"F0.wireOp",EDGE,"E113"),sQuery(id+"F0.wireOp",EDGE,"E114"),sQuery(id+"F0.wireOp",EDGE,"E115"),sQuery(id+"F0.wireOp",EDGE,"E116"),sQuery(id+"F0.wireOp",EDGE,"E117"),sQuery(id+"F0.wireOp",EDGE,"E118"),sQuery(id+"F0.wireOp",EDGE,"E119"),sQuery(id+"F0.wireOp",EDGE,"E120"),sQuery(id+"F0.wireOp",EDGE,"E121"),sQuery(id+"F0.wireOp",EDGE,"E122"),sQuery(id+"F0.wireOp",EDGE,"E123"),sQuery(id+"F0.wireOp",EDGE,"E124"),sQuery(id+"F0.wireOp",EDGE,"E125"),sQuery(id+"F0.wireOp",EDGE,"E126"),sQuery(id+"F0.wireOp",EDGE,"E127"),sQuery(id+"F0.wireOp",EDGE,"E128"),sQuery(id+"F0.wireOp",EDGE,"E129"),sQuery(id+"F0.wireOp",EDGE,"E130.trimOffspring"),sQuery(id+"F0.wireOp",EDGE,"E132.trimOffspring"),sQuery(id+"F0.wireOp",EDGE,"E134.trimOffspring"),sQuery(id+"F0.wireOp",EDGE,"E137.trimOffspring"),sQuery(id+"F0.wireOp",EDGE,"E138.trimOffspring"),sQuery(id+"F0.wireOp",EDGE,"E140.trimOffspring"),sQuery(id+"F0.wireOp",EDGE,"E142.trimOffspring"),sQuery(id+"F0.wireOp",EDGE,"E145.trimOffspring"),sQuery(id+"F0.wireOp",EDGE,"E146.trimOffspring"),sQuery(id+"F0.wireOp",EDGE,"E149.trimOffspring"),sQuery(id+"F0.wireOp",EDGE,"E150.trimOffspring"),sQuery(id+"F0.wireOp",EDGE,"E153.trimOffspring"),sQuery(id+"F0.wireOp",EDGE,"E154.trimOffspring"),sQuery(id+"F0.wireOp",EDGE,"E157.trimOffspring"),sQuery(id+"F0.wireOp",EDGE,"E158.trimOffspring"),sQuery(id+"F0.wireOp",EDGE,"E161.trimOffspring"),sQuery(id+"F0.wireOp",EDGE,"E162.trimOffspring"),sQuery(id+"F0.wireOp",EDGE,"E164.trimOffspring"),sQuery(id+"F0.wireOp",EDGE,"E166.trimOffspring"),sQuery(id+"F0.wireOp",EDGE,"E169.trimOffspring"),sQuery(id+"F0.wireOp",EDGE,"E170.trimOffspring"),sQuery(id+"F0.wireOp",EDGE,"E173.trimOffspring"),sQuery(id+"F0.wireOp",EDGE,"E175.trimOffspring"),sQuery(id+"F0.wireOp",EDGE,"E177.trimOffspring"),sQuery(id+"F0.wireOp",EDGE,"E179.trimOffspring"),sQuery(id+"F0.wireOp",EDGE,"E180.trimOffspring"),sQuery(id+"F0.wireOp",EDGE,"E182.trimOffspring"),sQuery(id+"F0.wireOp",EDGE,"E185.trimOffspring"),sQuery(id+"F0.wireOp",EDGE,"E186.trimOffspring"),sQuery(id+"F0.wireOp",EDGE,"E189.trimOffspring"),sQuery(id+"F0.wireOp",EDGE,"E190.trimOffspring"),sQuery(id+"F0.wireOp",EDGE,"E193.trimOffspring"),sQuery(id+"F0.wireOp",EDGE,"E194.trimOffspring"),sQuery(id+"F0.wireOp",EDGE,"E197.trimOffspring"),sQuery(id+"F0.wireOp",EDGE,"E198.trimOffspring"),sQuery(id+"F0.wireOp",EDGE,"E201.trimOffspring"),sQuery(id+"F0.wireOp",EDGE,"E202.trimOffspring"),sQuery(id+"F0.wireOp",EDGE,"E205.trimOffspring"),sQuery(id+"F0.wireOp",EDGE,"E206.trimOffspring"),sQuery(id+"F0.wireOp",EDGE,"E209.trimOffspring"),sQuery(id+"F0.wireOp",EDGE,"E211.trimOffspring"),sQuery(id+"F0.wireOp",EDGE,"E213.trimOffspring"),sQuery(id+"F0.wireOp",EDGE,"E215.trimOffspring"),sQuery(id+"F0.wireOp",EDGE,"E217.trimOffspring"),sQuery(id+"F0.wireOp",EDGE,"E219.trimOffspring"),sQuery(id+"F0.wireOp",EDGE,"E221.trimOffspring"),sQuery(id+"F0.wireOp",EDGE,"E223.trimOffspring"),sQuery(id+"F0.wireOp",EDGE,"E225.trimOffspring"),sQuery(id+"F0.wireOp",EDGE,"E226.trimOffspring"),sQuery(id+"F0.wireOp",EDGE,"E229.trimOffspring"),sQuery(id+"F0.wireOp",EDGE,"E230.trimOffspring"),sQuery(id+"F0.wireOp",EDGE,"E233.trimOffspring"),sQuery(id+"F0.wireOp",EDGE,"E235.trimOffspring"),sQuery(id+"F0.wireOp",EDGE,"E236.trimOffspring"),sQuery(id+"F0.wireOp",EDGE,"E238.trimOffspring"),sQuery(id+"F0.wireOp",EDGE,"E241.trimOffspring"),sQuery(id+"F0.wireOp",EDGE,"E242.trimOffspring"),sQuery(id+"F0.wireOp",EDGE,"E245.trimOffspring"),sQuery(id+"F0.wireOp",EDGE,"E246.trimOffspring"),sQuery(id+"F0.wireOp",EDGE,"E249.trimOffspring"),sQuery(id+"F0.wireOp",EDGE,"E250.trimOffspring"),sQuery(id+"F0.wireOp",EDGE,"E253.trimOffspring"),sQuery(id+"F0.wireOp",EDGE,"E254.trimOffspring"),sQuery(id+"F0.wireOp",EDGE,"E257.trimOffspring")])],"isStart":false});
            var sketch = newSketch(context, id + "F2", { "sketchPlane" : qUnion([Q0])});
            skCircle(sketch, "E258", {"center": v(0, 0) * mm, "radius": 17.25 * mm});
            skPoint(sketch, "E258.first.point", {"position": v(-9.1, 14.66) * mm});
            skPoint(sketch, "E258.second.point", {"position": v(-7.13, 15.7) * mm});
            skPoint(sketch, "E258.third.point", {"position": v(-3.93, 16.8) * mm});
            skCircle(sketch, "E259", {"center": v(0, 0) * mm, "radius": 22.5 * mm});
            skSolve(sketch);
        }
        {
            var Q0;
            Q0 = qSketchRegion(id + "F2", true);
            extrude(context, id + "F3", {"entities" : qUnion([Q0]), "operationType" : NewBodyOperationType.ADD, "oppositeDirection" : true, "depth" : 5 * mm, "offsetDistance" : 25 * mm});
        }
        {
            var Q0;
            Q0=makeQuery(id+"F3.boolean.opBoolean","MERGE",FACE,{"derivedFrom":[makeQuery(id+"F1.opExtrude","CAP_FACE",FACE,{"disambiguationData":[OSD([sQuery(id+"F0.wireOp",EDGE,"E0"),sQuery(id+"F0.wireOp",EDGE,"E1"),sQuery(id+"F0.wireOp",EDGE,"E2"),sQuery(id+"F0.wireOp",EDGE,"E3"),sQuery(id+"F0.wireOp",EDGE,"E4"),sQuery(id+"F0.wireOp",EDGE,"E5"),sQuery(id+"F0.wireOp",EDGE,"E6"),sQuery(id+"F0.wireOp",EDGE,"E7"),sQuery(id+"F0.wireOp",EDGE,"E8"),sQuery(id+"F0.wireOp",EDGE,"E9"),sQuery(id+"F0.wireOp",EDGE,"E10"),sQuery(id+"F0.wireOp",EDGE,"E11"),sQuery(id+"F0.wireOp",EDGE,"E12"),sQuery(id+"F0.wireOp",EDGE,"E13"),sQuery(id+"F0.wireOp",EDGE,"E14"),sQuery(id+"F0.wireOp",EDGE,"E15"),sQuery(id+"F0.wireOp",EDGE,"E16"),sQuery(id+"F0.wireOp",EDGE,"E17"),sQuery(id+"F0.wireOp",EDGE,"E18"),sQuery(id+"F0.wireOp",EDGE,"E19"),sQuery(id+"F0.wireOp",EDGE,"E20"),sQuery(id+"F0.wireOp",EDGE,"E21"),sQuery(id+"F0.wireOp",EDGE,"E22"),sQuery(id+"F0.wireOp",EDGE,"E23"),sQuery(id+"F0.wireOp",EDGE,"E24"),sQuery(id+"F0.wireOp",EDGE,"E25"),sQuery(id+"F0.wireOp",EDGE,"E26"),sQuery(id+"F0.wireOp",EDGE,"E27"),sQuery(id+"F0.wireOp",EDGE,"E28"),sQuery(id+"F0.wireOp",EDGE,"E29"),sQuery(id+"F0.wireOp",EDGE,"E30"),sQuery(id+"F0.wireOp",EDGE,"E31"),sQuery(id+"F0.wireOp",EDGE,"E32"),sQuery(id+"F0.wireOp",EDGE,"E33"),sQuery(id+"F0.wireOp",EDGE,"E34"),sQuery(id+"F0.wireOp",EDGE,"E35"),sQuery(id+"F0.wireOp",EDGE,"E36"),sQuery(id+"F0.wireOp",EDGE,"E37"),sQuery(id+"F0.wireOp",EDGE,"E38"),sQuery(id+"F0.wireOp",EDGE,"E39"),sQuery(id+"F0.wireOp",EDGE,"E40"),sQuery(id+"F0.wireOp",EDGE,"E41"),sQuery(id+"F0.wireOp",EDGE,"E42"),sQuery(id+"F0.wireOp",EDGE,"E43"),sQuery(id+"F0.wireOp",EDGE,"E44"),sQuery(id+"F0.wireOp",EDGE,"E45"),sQuery(id+"F0.wireOp",EDGE,"E46"),sQuery(id+"F0.wireOp",EDGE,"E47"),sQuery(id+"F0.wireOp",EDGE,"E48"),sQuery(id+"F0.wireOp",EDGE,"E49"),sQuery(id+"F0.wireOp",EDGE,"E50"),sQuery(id+"F0.wireOp",EDGE,"E51"),sQuery(id+"F0.wireOp",EDGE,"E52"),sQuery(id+"F0.wireOp",EDGE,"E53"),sQuery(id+"F0.wireOp",EDGE,"E54"),sQuery(id+"F0.wireOp",EDGE,"E55"),sQuery(id+"F0.wireOp",EDGE,"E56"),sQuery(id+"F0.wireOp",EDGE,"E57"),sQuery(id+"F0.wireOp",EDGE,"E58"),sQuery(id+"F0.wireOp",EDGE,"E59"),sQuery(id+"F0.wireOp",EDGE,"E60"),sQuery(id+"F0.wireOp",EDGE,"E61"),sQuery(id+"F0.wireOp",EDGE,"E62"),sQuery(id+"F0.wireOp",EDGE,"E63"),sQuery(id+"F0.wireOp",EDGE,"E64"),sQuery(id+"F0.wireOp",EDGE,"E65"),sQuery(id+"F0.wireOp",EDGE,"E66"),sQuery(id+"F0.wireOp",EDGE,"E67"),sQuery(id+"F0.wireOp",EDGE,"E68"),sQuery(id+"F0.wireOp",EDGE,"E69"),sQuery(id+"F0.wireOp",EDGE,"E70"),sQuery(id+"F0.wireOp",EDGE,"E71"),sQuery(id+"F0.wireOp",EDGE,"E72"),sQuery(id+"F0.wireOp",EDGE,"E73"),sQuery(id+"F0.wireOp",EDGE,"E74"),sQuery(id+"F0.wireOp",EDGE,"E75"),sQuery(id+"F0.wireOp",EDGE,"E76"),sQuery(id+"F0.wireOp",EDGE,"E77"),sQuery(id+"F0.wireOp",EDGE,"E78"),sQuery(id+"F0.wireOp",EDGE,"E79"),sQuery(id+"F0.wireOp",EDGE,"E80"),sQuery(id+"F0.wireOp",EDGE,"E81"),sQuery(id+"F0.wireOp",EDGE,"E82"),sQuery(id+"F0.wireOp",EDGE,"E83"),sQuery(id+"F0.wireOp",EDGE,"E84"),sQuery(id+"F0.wireOp",EDGE,"E85"),sQuery(id+"F0.wireOp",EDGE,"E86"),sQuery(id+"F0.wireOp",EDGE,"E87"),sQuery(id+"F0.wireOp",EDGE,"E88"),sQuery(id+"F0.wireOp",EDGE,"E89"),sQuery(id+"F0.wireOp",EDGE,"E90"),sQuery(id+"F0.wireOp",EDGE,"E91"),sQuery(id+"F0.wireOp",EDGE,"E92"),sQuery(id+"F0.wireOp",EDGE,"E93"),sQuery(id+"F0.wireOp",EDGE,"E94"),sQuery(id+"F0.wireOp",EDGE,"E95"),sQuery(id+"F0.wireOp",EDGE,"E96"),sQuery(id+"F0.wireOp",EDGE,"E97"),sQuery(id+"F0.wireOp",EDGE,"E98"),sQuery(id+"F0.wireOp",EDGE,"E99"),sQuery(id+"F0.wireOp",EDGE,"E100"),sQuery(id+"F0.wireOp",EDGE,"E101"),sQuery(id+"F0.wireOp",EDGE,"E102"),sQuery(id+"F0.wireOp",EDGE,"E103"),sQuery(id+"F0.wireOp",EDGE,"E104"),sQuery(id+"F0.wireOp",EDGE,"E105"),sQuery(id+"F0.wireOp",EDGE,"E106"),sQuery(id+"F0.wireOp",EDGE,"E107"),sQuery(id+"F0.wireOp",EDGE,"E108"),sQuery(id+"F0.wireOp",EDGE,"E109"),sQuery(id+"F0.wireOp",EDGE,"E110"),sQuery(id+"F0.wireOp",EDGE,"E111"),sQuery(id+"F0.wireOp",EDGE,"E112"),sQuery(id+"F0.wireOp",EDGE,"E113"),sQuery(id+"F0.wireOp",EDGE,"E114"),sQuery(id+"F0.wireOp",EDGE,"E115"),sQuery(id+"F0.wireOp",EDGE,"E116"),sQuery(id+"F0.wireOp",EDGE,"E117"),sQuery(id+"F0.wireOp",EDGE,"E118"),sQuery(id+"F0.wireOp",EDGE,"E119"),sQuery(id+"F0.wireOp",EDGE,"E120"),sQuery(id+"F0.wireOp",EDGE,"E121"),sQuery(id+"F0.wireOp",EDGE,"E122"),sQuery(id+"F0.wireOp",EDGE,"E123"),sQuery(id+"F0.wireOp",EDGE,"E124"),sQuery(id+"F0.wireOp",EDGE,"E125"),sQuery(id+"F0.wireOp",EDGE,"E126"),sQuery(id+"F0.wireOp",EDGE,"E127"),sQuery(id+"F0.wireOp",EDGE,"E128"),sQuery(id+"F0.wireOp",EDGE,"E129"),sQuery(id+"F0.wireOp",EDGE,"E130.trimOffspring"),sQuery(id+"F0.wireOp",EDGE,"E132.trimOffspring"),sQuery(id+"F0.wireOp",EDGE,"E134.trimOffspring"),sQuery(id+"F0.wireOp",EDGE,"E137.trimOffspring"),sQuery(id+"F0.wireOp",EDGE,"E138.trimOffspring"),sQuery(id+"F0.wireOp",EDGE,"E140.trimOffspring"),sQuery(id+"F0.wireOp",EDGE,"E142.trimOffspring"),sQuery(id+"F0.wireOp",EDGE,"E145.trimOffspring"),sQuery(id+"F0.wireOp",EDGE,"E146.trimOffspring"),sQuery(id+"F0.wireOp",EDGE,"E149.trimOffspring"),sQuery(id+"F0.wireOp",EDGE,"E150.trimOffspring"),sQuery(id+"F0.wireOp",EDGE,"E153.trimOffspring"),sQuery(id+"F0.wireOp",EDGE,"E154.trimOffspring"),sQuery(id+"F0.wireOp",EDGE,"E157.trimOffspring"),sQuery(id+"F0.wireOp",EDGE,"E158.trimOffspring"),sQuery(id+"F0.wireOp",EDGE,"E161.trimOffspring"),sQuery(id+"F0.wireOp",EDGE,"E162.trimOffspring"),sQuery(id+"F0.wireOp",EDGE,"E164.trimOffspring"),sQuery(id+"F0.wireOp",EDGE,"E166.trimOffspring"),sQuery(id+"F0.wireOp",EDGE,"E169.trimOffspring"),sQuery(id+"F0.wireOp",EDGE,"E170.trimOffspring"),sQuery(id+"F0.wireOp",EDGE,"E173.trimOffspring"),sQuery(id+"F0.wireOp",EDGE,"E175.trimOffspring"),sQuery(id+"F0.wireOp",EDGE,"E177.trimOffspring"),sQuery(id+"F0.wireOp",EDGE,"E179.trimOffspring"),sQuery(id+"F0.wireOp",EDGE,"E180.trimOffspring"),sQuery(id+"F0.wireOp",EDGE,"E182.trimOffspring"),sQuery(id+"F0.wireOp",EDGE,"E185.trimOffspring"),sQuery(id+"F0.wireOp",EDGE,"E186.trimOffspring"),sQuery(id+"F0.wireOp",EDGE,"E189.trimOffspring"),sQuery(id+"F0.wireOp",EDGE,"E190.trimOffspring"),sQuery(id+"F0.wireOp",EDGE,"E193.trimOffspring"),sQuery(id+"F0.wireOp",EDGE,"E194.trimOffspring"),sQuery(id+"F0.wireOp",EDGE,"E197.trimOffspring"),sQuery(id+"F0.wireOp",EDGE,"E198.trimOffspring"),sQuery(id+"F0.wireOp",EDGE,"E201.trimOffspring"),sQuery(id+"F0.wireOp",EDGE,"E202.trimOffspring"),sQuery(id+"F0.wireOp",EDGE,"E205.trimOffspring"),sQuery(id+"F0.wireOp",EDGE,"E206.trimOffspring"),sQuery(id+"F0.wireOp",EDGE,"E209.trimOffspring"),sQuery(id+"F0.wireOp",EDGE,"E211.trimOffspring"),sQuery(id+"F0.wireOp",EDGE,"E213.trimOffspring"),sQuery(id+"F0.wireOp",EDGE,"E215.trimOffspring"),sQuery(id+"F0.wireOp",EDGE,"E217.trimOffspring"),sQuery(id+"F0.wireOp",EDGE,"E219.trimOffspring"),sQuery(id+"F0.wireOp",EDGE,"E221.trimOffspring"),sQuery(id+"F0.wireOp",EDGE,"E223.trimOffspring"),sQuery(id+"F0.wireOp",EDGE,"E225.trimOffspring"),sQuery(id+"F0.wireOp",EDGE,"E226.trimOffspring"),sQuery(id+"F0.wireOp",EDGE,"E229.trimOffspring"),sQuery(id+"F0.wireOp",EDGE,"E230.trimOffspring"),sQuery(id+"F0.wireOp",EDGE,"E233.trimOffspring"),sQuery(id+"F0.wireOp",EDGE,"E235.trimOffspring"),sQuery(id+"F0.wireOp",EDGE,"E236.trimOffspring"),sQuery(id+"F0.wireOp",EDGE,"E238.trimOffspring"),sQuery(id+"F0.wireOp",EDGE,"E241.trimOffspring"),sQuery(id+"F0.wireOp",EDGE,"E242.trimOffspring"),sQuery(id+"F0.wireOp",EDGE,"E245.trimOffspring"),sQuery(id+"F0.wireOp",EDGE,"E246.trimOffspring"),sQuery(id+"F0.wireOp",EDGE,"E249.trimOffspring"),sQuery(id+"F0.wireOp",EDGE,"E250.trimOffspring"),sQuery(id+"F0.wireOp",EDGE,"E253.trimOffspring"),sQuery(id+"F0.wireOp",EDGE,"E254.trimOffspring"),sQuery(id+"F0.wireOp",EDGE,"E257.trimOffspring")])],"isStart":false}),makeQuery(id+"F3.opExtrude","CAP_FACE",FACE,{"disambiguationData":[OSD([sQuery(id+"F2.wireOp",EDGE,"E258"),sQuery(id+"F2.wireOp",EDGE,"E259")])],"isStart":true})]});
            var sketch = newSketch(context, id + "F4", { "sketchPlane" : qUnion([Q0])});
            skCircle(sketch, "E260", {"center": v(0, 0) * mm, "radius": 22.5 * mm});
            skPoint(sketch, "E260.first.point", {"position": v(-20.12, 10.06) * mm});
            skPoint(sketch, "E260.second.point", {"position": v(-17.52, 14.12) * mm});
            skPoint(sketch, "E260.third.point", {"position": v(-13.85, 17.73) * mm});
            skCircle(sketch, "E261", {"center": v(0, 0) * mm, "radius": 18 * mm});
            skSolve(sketch);
        }
        {
            var Q0;
            Q0 = qSketchRegion(id + "F4", true);
            extrude(context, id + "F5", {"entities" : qUnion([Q0]), "operationType" : NewBodyOperationType.REMOVE, "oppositeDirection" : true, "depth" : 25 * mm, "offsetDistance" : 25 * mm});
        }
        {
            var Q0;
            Q0=makeQuery(id+"F3.boolean.opBoolean","MERGE",FACE,{"derivedFrom":[makeQuery(id+"F1.opExtrude","CAP_FACE",FACE,{"disambiguationData":[OSD([sQuery(id+"F0.wireOp",EDGE,"E0"),sQuery(id+"F0.wireOp",EDGE,"E1"),sQuery(id+"F0.wireOp",EDGE,"E2"),sQuery(id+"F0.wireOp",EDGE,"E3"),sQuery(id+"F0.wireOp",EDGE,"E4"),sQuery(id+"F0.wireOp",EDGE,"E5"),sQuery(id+"F0.wireOp",EDGE,"E6"),sQuery(id+"F0.wireOp",EDGE,"E7"),sQuery(id+"F0.wireOp",EDGE,"E8"),sQuery(id+"F0.wireOp",EDGE,"E9"),sQuery(id+"F0.wireOp",EDGE,"E10"),sQuery(id+"F0.wireOp",EDGE,"E11"),sQuery(id+"F0.wireOp",EDGE,"E12"),sQuery(id+"F0.wireOp",EDGE,"E13"),sQuery(id+"F0.wireOp",EDGE,"E14"),sQuery(id+"F0.wireOp",EDGE,"E15"),sQuery(id+"F0.wireOp",EDGE,"E16"),sQuery(id+"F0.wireOp",EDGE,"E17"),sQuery(id+"F0.wireOp",EDGE,"E18"),sQuery(id+"F0.wireOp",EDGE,"E19"),sQuery(id+"F0.wireOp",EDGE,"E20"),sQuery(id+"F0.wireOp",EDGE,"E21"),sQuery(id+"F0.wireOp",EDGE,"E22"),sQuery(id+"F0.wireOp",EDGE,"E23"),sQuery(id+"F0.wireOp",EDGE,"E24"),sQuery(id+"F0.wireOp",EDGE,"E25"),sQuery(id+"F0.wireOp",EDGE,"E26"),sQuery(id+"F0.wireOp",EDGE,"E27"),sQuery(id+"F0.wireOp",EDGE,"E28"),sQuery(id+"F0.wireOp",EDGE,"E29"),sQuery(id+"F0.wireOp",EDGE,"E30"),sQuery(id+"F0.wireOp",EDGE,"E31"),sQuery(id+"F0.wireOp",EDGE,"E32"),sQuery(id+"F0.wireOp",EDGE,"E33"),sQuery(id+"F0.wireOp",EDGE,"E34"),sQuery(id+"F0.wireOp",EDGE,"E35"),sQuery(id+"F0.wireOp",EDGE,"E36"),sQuery(id+"F0.wireOp",EDGE,"E37"),sQuery(id+"F0.wireOp",EDGE,"E38"),sQuery(id+"F0.wireOp",EDGE,"E39"),sQuery(id+"F0.wireOp",EDGE,"E40"),sQuery(id+"F0.wireOp",EDGE,"E41"),sQuery(id+"F0.wireOp",EDGE,"E42"),sQuery(id+"F0.wireOp",EDGE,"E43"),sQuery(id+"F0.wireOp",EDGE,"E44"),sQuery(id+"F0.wireOp",EDGE,"E45"),sQuery(id+"F0.wireOp",EDGE,"E46"),sQuery(id+"F0.wireOp",EDGE,"E47"),sQuery(id+"F0.wireOp",EDGE,"E48"),sQuery(id+"F0.wireOp",EDGE,"E49"),sQuery(id+"F0.wireOp",EDGE,"E50"),sQuery(id+"F0.wireOp",EDGE,"E51"),sQuery(id+"F0.wireOp",EDGE,"E52"),sQuery(id+"F0.wireOp",EDGE,"E53"),sQuery(id+"F0.wireOp",EDGE,"E54"),sQuery(id+"F0.wireOp",EDGE,"E55"),sQuery(id+"F0.wireOp",EDGE,"E56"),sQuery(id+"F0.wireOp",EDGE,"E57"),sQuery(id+"F0.wireOp",EDGE,"E58"),sQuery(id+"F0.wireOp",EDGE,"E59"),sQuery(id+"F0.wireOp",EDGE,"E60"),sQuery(id+"F0.wireOp",EDGE,"E61"),sQuery(id+"F0.wireOp",EDGE,"E62"),sQuery(id+"F0.wireOp",EDGE,"E63"),sQuery(id+"F0.wireOp",EDGE,"E64"),sQuery(id+"F0.wireOp",EDGE,"E65"),sQuery(id+"F0.wireOp",EDGE,"E66"),sQuery(id+"F0.wireOp",EDGE,"E67"),sQuery(id+"F0.wireOp",EDGE,"E68"),sQuery(id+"F0.wireOp",EDGE,"E69"),sQuery(id+"F0.wireOp",EDGE,"E70"),sQuery(id+"F0.wireOp",EDGE,"E71"),sQuery(id+"F0.wireOp",EDGE,"E72"),sQuery(id+"F0.wireOp",EDGE,"E73"),sQuery(id+"F0.wireOp",EDGE,"E74"),sQuery(id+"F0.wireOp",EDGE,"E75"),sQuery(id+"F0.wireOp",EDGE,"E76"),sQuery(id+"F0.wireOp",EDGE,"E77"),sQuery(id+"F0.wireOp",EDGE,"E78"),sQuery(id+"F0.wireOp",EDGE,"E79"),sQuery(id+"F0.wireOp",EDGE,"E80"),sQuery(id+"F0.wireOp",EDGE,"E81"),sQuery(id+"F0.wireOp",EDGE,"E82"),sQuery(id+"F0.wireOp",EDGE,"E83"),sQuery(id+"F0.wireOp",EDGE,"E84"),sQuery(id+"F0.wireOp",EDGE,"E85"),sQuery(id+"F0.wireOp",EDGE,"E86"),sQuery(id+"F0.wireOp",EDGE,"E87"),sQuery(id+"F0.wireOp",EDGE,"E88"),sQuery(id+"F0.wireOp",EDGE,"E89"),sQuery(id+"F0.wireOp",EDGE,"E90"),sQuery(id+"F0.wireOp",EDGE,"E91"),sQuery(id+"F0.wireOp",EDGE,"E92"),sQuery(id+"F0.wireOp",EDGE,"E93"),sQuery(id+"F0.wireOp",EDGE,"E94"),sQuery(id+"F0.wireOp",EDGE,"E95"),sQuery(id+"F0.wireOp",EDGE,"E96"),sQuery(id+"F0.wireOp",EDGE,"E97"),sQuery(id+"F0.wireOp",EDGE,"E98"),sQuery(id+"F0.wireOp",EDGE,"E99"),sQuery(id+"F0.wireOp",EDGE,"E100"),sQuery(id+"F0.wireOp",EDGE,"E101"),sQuery(id+"F0.wireOp",EDGE,"E102"),sQuery(id+"F0.wireOp",EDGE,"E103"),sQuery(id+"F0.wireOp",EDGE,"E104"),sQuery(id+"F0.wireOp",EDGE,"E105"),sQuery(id+"F0.wireOp",EDGE,"E106"),sQuery(id+"F0.wireOp",EDGE,"E107"),sQuery(id+"F0.wireOp",EDGE,"E108"),sQuery(id+"F0.wireOp",EDGE,"E109"),sQuery(id+"F0.wireOp",EDGE,"E110"),sQuery(id+"F0.wireOp",EDGE,"E111"),sQuery(id+"F0.wireOp",EDGE,"E112"),sQuery(id+"F0.wireOp",EDGE,"E113"),sQuery(id+"F0.wireOp",EDGE,"E114"),sQuery(id+"F0.wireOp",EDGE,"E115"),sQuery(id+"F0.wireOp",EDGE,"E116"),sQuery(id+"F0.wireOp",EDGE,"E117"),sQuery(id+"F0.wireOp",EDGE,"E118"),sQuery(id+"F0.wireOp",EDGE,"E119"),sQuery(id+"F0.wireOp",EDGE,"E120"),sQuery(id+"F0.wireOp",EDGE,"E121"),sQuery(id+"F0.wireOp",EDGE,"E122"),sQuery(id+"F0.wireOp",EDGE,"E123"),sQuery(id+"F0.wireOp",EDGE,"E124"),sQuery(id+"F0.wireOp",EDGE,"E125"),sQuery(id+"F0.wireOp",EDGE,"E126"),sQuery(id+"F0.wireOp",EDGE,"E127"),sQuery(id+"F0.wireOp",EDGE,"E128"),sQuery(id+"F0.wireOp",EDGE,"E129"),sQuery(id+"F0.wireOp",EDGE,"E130.trimOffspring"),sQuery(id+"F0.wireOp",EDGE,"E132.trimOffspring"),sQuery(id+"F0.wireOp",EDGE,"E134.trimOffspring"),sQuery(id+"F0.wireOp",EDGE,"E137.trimOffspring"),sQuery(id+"F0.wireOp",EDGE,"E138.trimOffspring"),sQuery(id+"F0.wireOp",EDGE,"E140.trimOffspring"),sQuery(id+"F0.wireOp",EDGE,"E142.trimOffspring"),sQuery(id+"F0.wireOp",EDGE,"E145.trimOffspring"),sQuery(id+"F0.wireOp",EDGE,"E146.trimOffspring"),sQuery(id+"F0.wireOp",EDGE,"E149.trimOffspring"),sQuery(id+"F0.wireOp",EDGE,"E150.trimOffspring"),sQuery(id+"F0.wireOp",EDGE,"E153.trimOffspring"),sQuery(id+"F0.wireOp",EDGE,"E154.trimOffspring"),sQuery(id+"F0.wireOp",EDGE,"E157.trimOffspring"),sQuery(id+"F0.wireOp",EDGE,"E158.trimOffspring"),sQuery(id+"F0.wireOp",EDGE,"E161.trimOffspring"),sQuery(id+"F0.wireOp",EDGE,"E162.trimOffspring"),sQuery(id+"F0.wireOp",EDGE,"E164.trimOffspring"),sQuery(id+"F0.wireOp",EDGE,"E166.trimOffspring"),sQuery(id+"F0.wireOp",EDGE,"E169.trimOffspring"),sQuery(id+"F0.wireOp",EDGE,"E170.trimOffspring"),sQuery(id+"F0.wireOp",EDGE,"E173.trimOffspring"),sQuery(id+"F0.wireOp",EDGE,"E175.trimOffspring"),sQuery(id+"F0.wireOp",EDGE,"E177.trimOffspring"),sQuery(id+"F0.wireOp",EDGE,"E179.trimOffspring"),sQuery(id+"F0.wireOp",EDGE,"E180.trimOffspring"),sQuery(id+"F0.wireOp",EDGE,"E182.trimOffspring"),sQuery(id+"F0.wireOp",EDGE,"E185.trimOffspring"),sQuery(id+"F0.wireOp",EDGE,"E186.trimOffspring"),sQuery(id+"F0.wireOp",EDGE,"E189.trimOffspring"),sQuery(id+"F0.wireOp",EDGE,"E190.trimOffspring"),sQuery(id+"F0.wireOp",EDGE,"E193.trimOffspring"),sQuery(id+"F0.wireOp",EDGE,"E194.trimOffspring"),sQuery(id+"F0.wireOp",EDGE,"E197.trimOffspring"),sQuery(id+"F0.wireOp",EDGE,"E198.trimOffspring"),sQuery(id+"F0.wireOp",EDGE,"E201.trimOffspring"),sQuery(id+"F0.wireOp",EDGE,"E202.trimOffspring"),sQuery(id+"F0.wireOp",EDGE,"E205.trimOffspring"),sQuery(id+"F0.wireOp",EDGE,"E206.trimOffspring"),sQuery(id+"F0.wireOp",EDGE,"E209.trimOffspring"),sQuery(id+"F0.wireOp",EDGE,"E211.trimOffspring"),sQuery(id+"F0.wireOp",EDGE,"E213.trimOffspring"),sQuery(id+"F0.wireOp",EDGE,"E215.trimOffspring"),sQuery(id+"F0.wireOp",EDGE,"E217.trimOffspring"),sQuery(id+"F0.wireOp",EDGE,"E219.trimOffspring"),sQuery(id+"F0.wireOp",EDGE,"E221.trimOffspring"),sQuery(id+"F0.wireOp",EDGE,"E223.trimOffspring"),sQuery(id+"F0.wireOp",EDGE,"E225.trimOffspring"),sQuery(id+"F0.wireOp",EDGE,"E226.trimOffspring"),sQuery(id+"F0.wireOp",EDGE,"E229.trimOffspring"),sQuery(id+"F0.wireOp",EDGE,"E230.trimOffspring"),sQuery(id+"F0.wireOp",EDGE,"E233.trimOffspring"),sQuery(id+"F0.wireOp",EDGE,"E235.trimOffspring"),sQuery(id+"F0.wireOp",EDGE,"E236.trimOffspring"),sQuery(id+"F0.wireOp",EDGE,"E238.trimOffspring"),sQuery(id+"F0.wireOp",EDGE,"E241.trimOffspring"),sQuery(id+"F0.wireOp",EDGE,"E242.trimOffspring"),sQuery(id+"F0.wireOp",EDGE,"E245.trimOffspring"),sQuery(id+"F0.wireOp",EDGE,"E246.trimOffspring"),sQuery(id+"F0.wireOp",EDGE,"E249.trimOffspring"),sQuery(id+"F0.wireOp",EDGE,"E250.trimOffspring"),sQuery(id+"F0.wireOp",EDGE,"E253.trimOffspring"),sQuery(id+"F0.wireOp",EDGE,"E254.trimOffspring"),sQuery(id+"F0.wireOp",EDGE,"E257.trimOffspring")])],"isStart":false}),makeQuery(id+"F3.opExtrude","CAP_FACE",FACE,{"disambiguationData":[OSD([sQuery(id+"F2.wireOp",EDGE,"E258"),sQuery(id+"F2.wireOp",EDGE,"E259")])],"isStart":true})]});
            var sketch = newSketch(context, id + "F6", { "sketchPlane" : qUnion([Q0])});
            skCircle(sketch, "E262", {"center": v(0, 0) * mm, "radius": 18 * mm});
            skPoint(sketch, "E262.first.point", {"position": v(-15.82, 8.58) * mm});
            skPoint(sketch, "E262.second.point", {"position": v(-15.43, 9.27) * mm});
            skPoint(sketch, "E262.third.point", {"position": v(-14.48, 10.7) * mm});
            skCircle(sketch, "E263", {"center": v(0, 0) * mm, "radius": 14 * mm});
            skSolve(sketch);
        }
        {
            var Q0;
            Q0 = qSketchRegion(id + "F6", true);
            extrude(context, id + "F7", {"entities" : qUnion([Q0]), "operationType" : NewBodyOperationType.ADD, "depth" : 5 * mm, "offsetDistance" : 25 * mm});
        }
        {
            var Q0;
            Q0=makeQuery(id+"F7.opExtrude","CAP_FACE",FACE,{"disambiguationData":[OSD([sQuery(id+"F6.wireOp",EDGE,"E262"),sQuery(id+"F6.wireOp",EDGE,"E263")])],"isStart":false});
            var sketch = newSketch(context, id + "F8", { "sketchPlane" : qUnion([Q0])});
            skCircle(sketch, "E264", {"center": v(0, 0) * mm, "radius": 18 * mm});
            skPoint(sketch, "E264.first.point", {"position": v(-15.92, 8.4) * mm});
            skPoint(sketch, "E264.second.point", {"position": v(-13.59, 11.8) * mm});
            skPoint(sketch, "E264.third.point", {"position": v(-10.23, 14.8) * mm});
            skSolve(sketch);
        }
        {
            var Q0;
            Q0 = qSketchRegion(id + "F8", true);
            extrude(context, id + "F9", {"entities" : qUnion([Q0]), "operationType" : NewBodyOperationType.ADD, "oppositeDirection" : true, "depth" : 2 * mm, "offsetDistance" : 25 * mm});
        }
        {
            var Q0;
            Q0=makeQuery(id+"F9.boolean.opBoolean","MERGE",FACE,{"derivedFrom":[makeQuery(id+"F7.opExtrude","CAP_FACE",FACE,{"disambiguationData":[OSD([sQuery(id+"F6.wireOp",EDGE,"E262"),sQuery(id+"F6.wireOp",EDGE,"E263")])],"isStart":false}),makeQuery(id+"F9.opExtrude","CAP_FACE",FACE,{"disambiguationData":[OSD([sQuery(id+"F8.wireOp",EDGE,"E264")])],"isStart":true})]});
            var sketch = newSketch(context, id + "F10", { "sketchPlane" : qUnion([Q0])});
            skCircle(sketch, "E265", {"center": v(0, 0) * mm, "radius": 4 * mm});
            skSolve(sketch);
        }
        {
            var Q0;
            Q0 = qSketchRegion(id + "F10", true);
            extrude(context, id + "F11", {"entities" : qUnion([Q0]), "operationType" : NewBodyOperationType.ADD, "oppositeDirection" : true, "depth" : 5 * mm, "offsetDistance" : 25 * mm});
        }
        {
            var Q0;
            Q0=makeQuery(id+"F9.boolean.opBoolean","MERGE",FACE,{"derivedFrom":[makeQuery(id+"F7.opExtrude","CAP_FACE",FACE,{"disambiguationData":[OSD([sQuery(id+"F6.wireOp",EDGE,"E262"),sQuery(id+"F6.wireOp",EDGE,"E263")])],"isStart":false}),makeQuery(id+"F9.opExtrude","CAP_FACE",FACE,{"disambiguationData":[OSD([sQuery(id+"F8.wireOp",EDGE,"E264")])],"isStart":true})]});
            var sketch = newSketch(context, id + "F12", { "sketchPlane" : qUnion([Q0])});
            skCircle(sketch, "E266", {"center": v(0, 0) * mm, "radius": 2.5 * mm});
            skSolve(sketch);
        }
        {
            var Q0;
            Q0 = qSketchRegion(id + "F12", true);
            extrude(context, id + "F13", {"entities" : qUnion([Q0]), "operationType" : NewBodyOperationType.REMOVE, "oppositeDirection" : true, "depth" : 25 * mm, "offsetDistance" : 25 * mm});
        }
        {
            var Q0;
            Q0=makeQuery(id+"F11.opExtrude","CAP_FACE",FACE,{"disambiguationData":[OSD([sQuery(id+"F10.wireOp",EDGE,"E265")])],"isStart":false});
            var sketch = newSketch(context, id + "F14", { "sketchPlane" : qUnion([Q0])});
            skCircle(sketch, "E267", {"center": v(0, 0) * mm, "radius": 4 * mm});
            skCircle(sketch, "E268", {"center": v(0, 0) * mm, "radius": 2 * mm});
            skSolve(sketch);
        }
        {
            var Q0;
            Q0 = qSketchRegion(id + "F14", true);
            extrude(context, id + "F15", {"entities" : qUnion([Q0]), "operationType" : NewBodyOperationType.ADD, "oppositeDirection" : true, "depth" : 1.5 * mm, "offsetDistance" : 25 * mm});
        }
        {
            var Q0;
            Q0=makeQuery(id+"F9.boolean.opBoolean","MERGE",FACE,{"derivedFrom":[makeQuery(id+"F7.opExtrude","CAP_FACE",FACE,{"disambiguationData":[OSD([sQuery(id+"F6.wireOp",EDGE,"E262"),sQuery(id+"F6.wireOp",EDGE,"E263")])],"isStart":false}),makeQuery(id+"F9.opExtrude","CAP_FACE",FACE,{"disambiguationData":[OSD([sQuery(id+"F8.wireOp",EDGE,"E264")])],"isStart":true})]});
            var sketch = newSketch(context, id + "F16", { "sketchPlane" : qUnion([Q0])});
            skCircle(sketch, "E269", {"center": v(0, 0) * mm, "radius": 2.5 * mm, "construction": true});
            skPoint(sketch, "E269.first.point", {"position": v(2.23, -1.14) * mm});
            skPoint(sketch, "E269.second.point", {"position": v(1.65, -1.88) * mm});
            skPoint(sketch, "E269.third.point", {"position": v(0.27, -2.49) * mm});
            skArc(sketch, "E270", {"start": v(66.57, 21.63) * mm, "mid": v(41.14, 56.63) * mm, "end": v(0, 70) * mm});
            skLineSegment(sketch, "E271", {"start": v(0, 0) * mm, "end": v(0, 70) * mm, "construction": true});
            skLineSegment(sketch, "E272", {"start": v(0, 0) * mm, "end": v(66.57, 21.63) * mm, "construction": true});
            skCircle(sketch, "E273", {"center": v(66.57, 21.63) * mm, "radius": 10 * mm, "construction": true});
            skArc(sketch, "E274", {"start": v(48.2, 23.15) * mm, "mid": v(56.24, 8.58) * mm, "end": v(66.57, 21.63) * mm});
            skLineSegment(sketch, "E275", {"start": v(7.8, -16.22) * mm, "end": v(61.4, 9.53) * mm});
            skCircle(sketch, "E276", {"center": v(0, 0) * mm, "radius": 18 * mm});
            skPoint(sketch, "E276.first.point", {"position": v(-2.6, -17.81) * mm});
            skPoint(sketch, "E276.second.point", {"position": v(-6.99, -16.59) * mm});
            skPoint(sketch, "E276.third.point", {"position": v(-10.1, -14.9) * mm});
            skArc(sketch, "E277", {"start": v(59.39, 8.56) * mm, "mid": v(39.28, 45.35) * mm, "end": v(0, 60) * mm});
            skLineSegment(sketch, "E278", {"start": v(0, 0) * mm, "end": v(2.25, 1.08) * mm});
            skLineSegment(sketch, "E279.trimOffspring", {"start": v(74.82, 15.98) * mm, "end": v(75.04, 16.08) * mm});
            skLineSegment(sketch, "E280.trimOffspring", {"start": v(16.22, 7.8) * mm, "end": v(54.08, 25.98) * mm});
            skLineSegment(sketch, "E281", {"start": v(0, 60) * mm, "end": v(0, 70) * mm, "construction": true});
            skArc(sketch, "E282", {"start": v(0, 70) * mm, "mid": v(-5, 65) * mm, "end": v(0, 60) * mm});
            skSolve(sketch);
        }
        {
            var Q0;
            {var subQ4=sQuery(id+"F16.wireOp",EDGE,"E270");Q0=makeQuery(id+"F16.imprint","IMPRINT",FACE,{"disambiguationData":[TD([[makeQuery(id+"F16.imprint","IMPRINT",EDGE,{"derivedFrom":subQ4}),1.0]])]});}
            var Q1;
            {var subQ0=sQuery(id+"F16.wireOp",EDGE,"E280.trimOffspring");var subQ1=sQuery(id+"F16.wireOp",EDGE,"E274");var subQ2=makeQuery(id+"F16.imprint","INTERSECT",VERTEX,{"derivedFrom":[subQ1,subQ0]});Q1=makeQuery(id+"F16.imprint","IMPRINT",FACE,{"disambiguationData":[TD([[makeQuery(id+"F16.imprint","IMPRINT",EDGE,{"disambiguationData":[TD([[subQ2,-1.0]])],"derivedFrom":subQ1}),1.0]])]});}
            var Q2;
            {var subQ0=sQuery(id+"F16.wireOp",EDGE,"E275");var subQ1=sQuery(id+"F16.wireOp",EDGE,"E274");var subQ2=makeQuery(id+"F16.imprint","INTERSECT",VERTEX,{"derivedFrom":[subQ1,subQ0]});Q2=makeQuery(id+"F16.imprint","IMPRINT",FACE,{"disambiguationData":[TD([[makeQuery(id+"F16.imprint","IMPRINT",EDGE,{"disambiguationData":[TD([[subQ2,1.0]])],"derivedFrom":subQ1}),-1.0]])]});}
            var Q3;
            {var subQ3=sQuery(id+"F16.wireOp",EDGE,"E274");var subQ7=sQuery(id+"F16.wireOp",EDGE,"E280.trimOffspring");var subQ9=makeQuery(id+"F16.imprint","INTERSECT",VERTEX,{"derivedFrom":[subQ3,subQ7]});Q3=makeQuery(id+"F16.imprint","IMPRINT",FACE,{"disambiguationData":[TD([[makeQuery(id+"F16.imprint","IMPRINT",EDGE,{"disambiguationData":[TD([[subQ9,-1.0]])],"derivedFrom":subQ3}),-1.0]])]});}
            extrude(context, id + "F17", {"entities" : qUnion([Q0, Q1, Q2, Q3]), "operationType" : NewBodyOperationType.ADD, "oppositeDirection" : true, "depth" : 7 * mm, "offsetDistance" : 25 * mm});
        }
        {
            var Q0;
            Q0=makeQuery(id+"F17.opExtrude","SWEPT_EDGE",EDGE,{"disambiguationData":[OSD([sQuery(id+"F16.wireOp",EDGE,"E276"),sQuery(id+"F16.wireOp",EDGE,"E280.trimOffspring")])]});
            var Q1;
            Q1=makeQuery(id+"F17.opExtrude","SWEPT_EDGE",EDGE,{"disambiguationData":[OSD([sQuery(id+"F16.wireOp",EDGE,"E277"),sQuery(id+"F16.wireOp",EDGE,"E280.trimOffspring")])]});
            fillet(context, id + "F18", {"entities" : qUnion([Q0, Q1]), "radius" : 10 * mm, "tangentPropagation" : true, "allowEdgeOverflow" : false});
        }
    });
